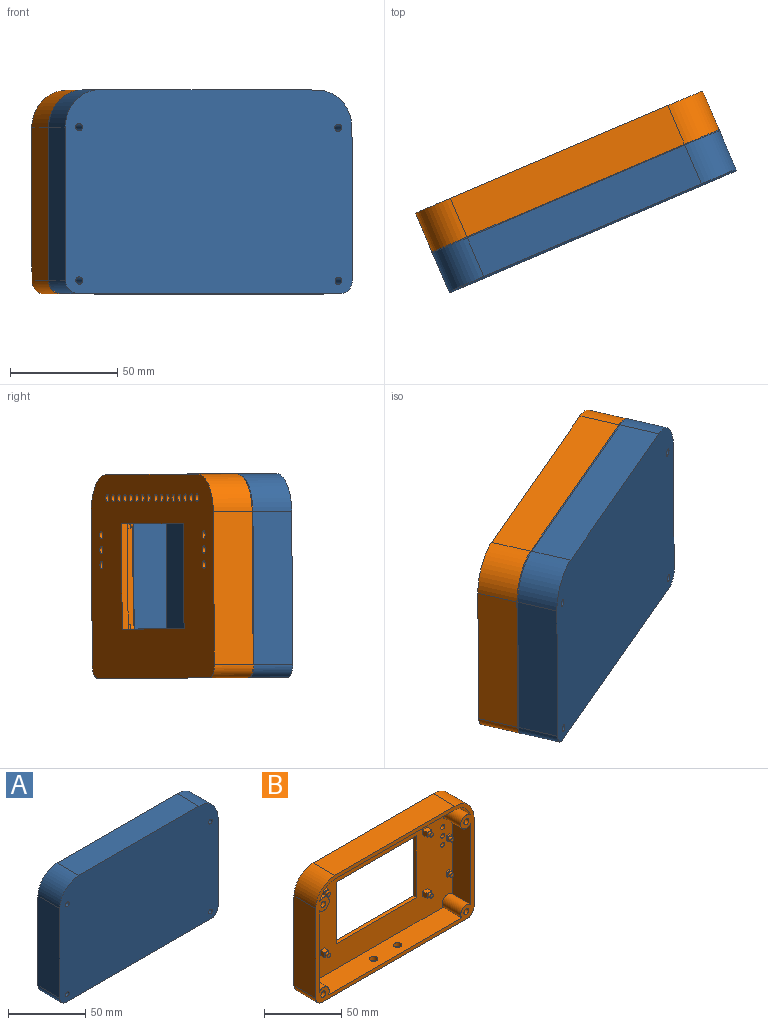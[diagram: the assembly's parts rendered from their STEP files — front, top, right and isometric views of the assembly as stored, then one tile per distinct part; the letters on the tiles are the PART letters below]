
ASSEMBLY  parts=2 mates=1
PART A: 51 faces, bbox 145x20x94.7 mm
  f0: plane 40x17mm, normal (0,0,1), area 624mm2, adj f3,f23,f28,f29,f33,f34,f35,f36
  f1: plane 36x17mm, normal (0,0,-1), area 556mm2, adj f3,f30,f31,f32,f33,f34,f35,f36
  f2: plane 41.8x17mm, normal (0,0,1), area 710.6mm2, adj f3,f23,f26,f29
  f3: plane 145x94.7mm, normal (0,1,0), area 1590.6mm2, adj f0,f1,f2,f4,f5,f6,f7,f8
  f4: plane 110x20mm, normal (0,0,1), area 2200mm2, adj f3,f5,f11,f12
  f5: cylinder r=17.5mm len=20mm, axis (0,1,0), area 549.8mm2, adj f3,f4,f6,f12
  f6: plane 71.2x20mm, normal (-1,0,0), area 1424mm2, adj f3,f5,f7,f12
  f7: cylinder r=6mm len=20mm, axis (0,1,0), area 188.5mm2, adj f3,f6,f8,f12
  f8: plane 133x20mm, normal (0,0,-1), area 2048mm2, adj f3,f7,f9,f12,f30,f31,f32
  f9: cylinder r=6mm len=20mm, axis (0,1,0), area 188.5mm2, adj f3,f8,f10,f12
  f10: plane 71.2x20mm, normal (1,0,0), area 1424mm2, adj f3,f9,f11,f12
  f11: cylinder r=17.5mm len=20mm, axis (0,1,0), area 549.8mm2, adj f3,f4,f10,f12
  f12: plane 145x94.7mm, normal (0,-1,0), area 13548.3mm2, adj f4,f5,f6,f7,f8,f9,f10,f11
  f13: cylinder r=1.7mm len=20mm, axis (0,-1,0), area 213.6mm2, adj f3,f12
  f14: cylinder r=1.7mm len=20mm, axis (0,-1,0), area 213.6mm2, adj f3,f12
  f15: cylinder r=1.7mm len=20mm, axis (0,-1,0), area 213.6mm2, adj f3,f12
  f16: cylinder r=1.7mm len=20mm, axis (0,-1,0), area 213.6mm2, adj f3,f12
  f17: plane 110x17mm, normal (0,0,-1), area 1870mm2, adj f3,f18,f22,f23
  f18: cylinder r=14.5mm len=17mm, axis (0,1,0), area 337.8mm2, adj f3,f17,f23,f24
  f19: plane 66.36x17mm, normal (1,0,0), area 1128.2mm2, adj f3,f23,f24,f26
  f20: plane 41.8x17mm, normal (0,0,1), area 710.6mm2, adj f3,f23,f25,f28
  f21: plane 66.36x17mm, normal (-1,0,0), area 1128.2mm2, adj f3,f23,f25,f27
  f22: cylinder r=14.5mm len=17mm, axis (0,1,0), area 337.8mm2, adj f3,f17,f23,f27
  f23: plane 139x88.7mm, normal (0,1,0), area 11201.7mm2, adj f0,f2,f17,f18,f19,f20,f21,f22
  f24: cylinder r=4.7mm len=17mm, axis (0,-1,0), area 405mm2, adj f3,f18,f19,f23
  f25: cylinder r=4.7mm len=17mm, axis (0,-1,0), area 260mm2, adj f3,f20,f21,f23
  f26: cylinder r=4.7mm len=17mm, axis (0,-1,0), area 260mm2, adj f2,f3,f19,f23
  f27: cylinder r=4.7mm len=17mm, axis (0,-1,0), area 405mm2, adj f3,f21,f22,f23
  f28: plane 17x17mm, normal (1,0,0), area 289mm2, adj f0,f3,f20,f23
  f29: plane 17x17mm, normal (-1,0,0), area 289mm2, adj f0,f2,f3,f23
  f30: plane 18x17mm, normal (1,0,0), area 306mm2, adj f1,f3,f8,f32
  f31: plane 18x17mm, normal (-1,0,0), area 306mm2, adj f1,f3,f8,f32
  f32: plane 36x18mm, normal (0,1,0), area 648mm2, adj f1,f8,f30,f31
  f33: plane 7x2mm, normal (0,1,0), area 14mm2, adj f0,f1,f34,f36
  f34: plane 4x2mm, normal (1,0,0), area 8mm2, adj f0,f1,f33,f35
  f35: plane 7x2mm, normal (0,-1,0), area 14mm2, adj f0,f1,f34,f36
  f36: plane 4x2mm, normal (-1,0,0), area 8mm2, adj f0,f1,f33,f35
  f37: plane 7x2mm, normal (0,1,0), area 14mm2, adj f0,f1,f38,f40
  f38: plane 4x2mm, normal (1,0,0), area 8mm2, adj f0,f1,f37,f39
  f39: plane 7x2mm, normal (0,-1,0), area 14mm2, adj f0,f1,f38,f40
  f40: plane 4x2mm, normal (-1,0,0), area 8mm2, adj f0,f1,f37,f39
  f41: plane 18x4mm, normal (0,0,-1), area 72mm2, adj f23,f42,f44,f45
  f42: plane 4x3mm, normal (-1,0,0), area 12mm2, adj f23,f41,f43,f45
  f43: plane 18x4mm, normal (0,0,1), area 72mm2, adj f23,f42,f44,f45
  f44: plane 4x3mm, normal (1,0,0), area 12mm2, adj f23,f41,f43,f45
  f45: plane 18x3mm, normal (0,1,0), area 54mm2, adj f41,f42,f43,f44
  f46: plane 4x3mm, normal (1,0,0), area 12mm2, adj f23,f47,f49,f50
  f47: plane 18x4mm, normal (0,0,-1), area 72mm2, adj f23,f46,f48,f50
  f48: plane 4x3mm, normal (-1,0,0), area 12mm2, adj f23,f47,f49,f50
  f49: plane 18x4mm, normal (0,0,1), area 72mm2, adj f23,f46,f48,f50
  f50: plane 18x3mm, normal (0,1,0), area 54mm2, adj f46,f47,f48,f49
PART B: 141 faces, bbox 145x20x94.7 mm
  f0: plane 145x94.7mm, normal (0,1,0), area 9777.3mm2, adj f2,f3,f4,f5,f6,f7,f8,f9
  f1: plane 139x88.7mm, normal (0,-1,0), area 7978.6mm2, adj f19,f20,f21,f22,f23,f24,f25,f26
  f2: plane 110x20mm, normal (0,0,1), area 2200mm2, adj f0,f3,f9,f10
  f3: cylinder r=17.5mm len=20mm, axis (0,1,0), area 549.8mm2, adj f0,f2,f4,f10
  f4: plane 71.2x20mm, normal (-1,0,0), area 1424mm2, adj f0,f3,f5,f10
  f5: cylinder r=6mm len=20mm, axis (0,1,0), area 188.5mm2, adj f0,f4,f6,f10
  f6: plane 133x20mm, normal (0,0,-1), area 2612.5mm2, adj f0,f5,f7,f10,f55,f56
  f7: cylinder r=6mm len=20mm, axis (0,1,0), area 188.5mm2, adj f0,f6,f8,f10
  f8: plane 71.2x20mm, normal (1,0,0), area 1424mm2, adj f0,f7,f9,f10
  f9: cylinder r=17.5mm len=20mm, axis (0,1,0), area 549.8mm2, adj f0,f2,f8,f10
  f10: plane 145x94.7mm, normal (0,-1,0), area 1575.1mm2, adj f2,f3,f4,f5,f6,f7,f8,f9
  f11: cone r=0mm half-angle=59deg, axis (0,-1,0), area 18.6mm2, adj f12
  f12: cylinder r=2.25mm len=17mm, axis (0,-1,0), area 240.3mm2, adj f10,f11
  f13: cone r=0mm half-angle=59deg, axis (0,-1,0), area 18.6mm2, adj f14
  f14: cylinder r=2.25mm len=17mm, axis (0,-1,0), area 240.3mm2, adj f10,f13
  f15: cone r=0mm half-angle=59deg, axis (0,-1,0), area 18.6mm2, adj f16
  f16: cylinder r=2.25mm len=17mm, axis (0,-1,0), area 240.3mm2, adj f10,f15
  f17: cone r=0mm half-angle=59deg, axis (0,-1,0), area 18.6mm2, adj f18
  f18: cylinder r=2.25mm len=17mm, axis (0,-1,0), area 240.3mm2, adj f10,f17
  f19: cylinder r=5.25mm len=17mm, axis (0,-1,0), area 269.7mm2, adj f1,f10,f23,f24
  f20: plane 110x17mm, normal (0,0,-1), area 1870mm2, adj f1,f10,f21,f25
  f21: cylinder r=14.5mm len=17mm, axis (0,1,0), area 319.1mm2, adj f1,f10,f20,f26
  f22: plane 64.5x17mm, normal (1,0,0), area 1096.5mm2, adj f1,f10,f26,f28
  f23: plane 122.25x17mm, normal (0,0,1), area 2030.7mm2, adj f1,f10,f19,f28,f55,f56
  f24: plane 64.5x17mm, normal (-1,0,0), area 1096.5mm2, adj f1,f10,f19,f27
  f25: cylinder r=14.5mm len=17mm, axis (0,1,0), area 319.1mm2, adj f1,f10,f20,f27
  f26: cylinder r=5.25mm len=17mm, axis (0,-1,0), area 421.7mm2, adj f1,f10,f21,f22
  f27: cylinder r=5.25mm len=17mm, axis (0,-1,0), area 421.7mm2, adj f1,f10,f24,f25
  f28: cylinder r=5.25mm len=17mm, axis (0,-1,0), area 269.7mm2, adj f1,f10,f22,f23
  f29: cylinder r=1.75mm len=3.5mm, axis (0,-1,0), area 33mm2, adj f0,f1
  f30: cylinder r=1.75mm len=3.5mm, axis (0,-1,0), area 33mm2, adj f0,f1
  f31: cylinder r=1.75mm len=3.5mm, axis (0,-1,0), area 33mm2, adj f0,f1
  f32: cylinder r=1.75mm len=3.5mm, axis (0,-1,0), area 33mm2, adj f0,f1
  f33: cylinder r=1.75mm len=3.5mm, axis (0,-1,0), area 33mm2, adj f0,f1
  f34: cylinder r=1.75mm len=3.5mm, axis (0,-1,0), area 33mm2, adj f0,f1
  f35: cylinder r=1.75mm len=3.5mm, axis (0,-1,0), area 33mm2, adj f0,f1
  f36: cylinder r=1.75mm len=3.5mm, axis (0,-1,0), area 33mm2, adj f0,f1
  f37: cylinder r=1.75mm len=3.5mm, axis (0,-1,0), area 33mm2, adj f0,f1
  f38: cylinder r=1.75mm len=3.5mm, axis (0,-1,0), area 33mm2, adj f0,f1
  f39: cylinder r=1.75mm len=3.5mm, axis (0,-1,0), area 33mm2, adj f0,f1
  f40: cylinder r=1.75mm len=3.5mm, axis (0,-1,0), area 33mm2, adj f0,f1
  f41: cylinder r=1.75mm len=3.5mm, axis (0,-1,0), area 33mm2, adj f0,f1
  f42: cylinder r=1.75mm len=3.5mm, axis (0,-1,0), area 33mm2, adj f0,f1
  f43: cylinder r=1.75mm len=3.5mm, axis (0,-1,0), area 33mm2, adj f0,f1
  f44: cylinder r=1.75mm len=3.5mm, axis (0,-1,0), area 33mm2, adj f0,f1
  f45: cylinder r=1.75mm len=3.5mm, axis (0,-1,0), area 33mm2, adj f0,f1
  f46: cylinder r=1.75mm len=3.5mm, axis (0,-1,0), area 33mm2, adj f0,f1
  f47: cylinder r=1.75mm len=3.5mm, axis (0,-1,0), area 33mm2, adj f0,f1
  f48: cylinder r=1.75mm len=3.5mm, axis (0,-1,0), area 33mm2, adj f0,f1
  f49: cylinder r=1.75mm len=3.5mm, axis (0,-1,0), area 33mm2, adj f0,f1
  f50: cylinder r=1.75mm len=3.5mm, axis (0,-1,0), area 33mm2, adj f0,f1
  f51: plane 73.44x3mm, normal (0,0,-1), area 220.3mm2, adj f0,f1,f52,f54
  f52: plane 48.96x3mm, normal (1,0,0), area 146.9mm2, adj f0,f1,f51,f53
  f53: plane 73.44x3mm, normal (0,0,1), area 220.3mm2, adj f0,f1,f52,f54
  f54: plane 48.96x3mm, normal (-1,0,0), area 146.9mm2, adj f0,f1,f51,f53
  f55: cylinder r=2.75mm len=5.5mm, axis (0,0,-1), area 51.8mm2, adj f6,f23
  f56: cylinder r=2.75mm len=5.5mm, axis (0,0,-1), area 51.8mm2, adj f6,f23
  f57: plane 3x1.5mm, normal (0,0,-1), area 4.5mm2, adj f1,f58,f60,f61
  f58: plane 4x1.5mm, normal (1,0,0), area 6mm2, adj f1,f57,f59,f61
  f59: plane 3x1.5mm, normal (0,0,1), area 4.5mm2, adj f1,f58,f60,f61
  f60: plane 4x1.5mm, normal (-1,0,0), area 6mm2, adj f1,f57,f59,f61
  f61: plane 4x3mm, normal (0,-1,0), area 5mm2, adj f57,f58,f59,f60,f99
  f62: plane 3x1.5mm, normal (0,0,-1), area 4.5mm2, adj f1,f63,f65,f66
  f63: plane 4x1.5mm, normal (1,0,0), area 6mm2, adj f1,f62,f64,f66
  f64: plane 3x1.5mm, normal (0,0,1), area 4.5mm2, adj f1,f63,f65,f66
  f65: plane 4x1.5mm, normal (-1,0,0), area 6mm2, adj f1,f62,f64,f66
  f66: plane 4x3mm, normal (0,-1,0), area 5mm2, adj f62,f63,f64,f65,f97
  f67: plane 3x1.5mm, normal (0,0,-1), area 4.5mm2, adj f1,f68,f70,f71
  f68: plane 4x1.5mm, normal (1,0,0), area 6mm2, adj f1,f67,f69,f71
  f69: plane 3x1.5mm, normal (0,0,1), area 4.5mm2, adj f1,f68,f70,f71
  f70: plane 4x1.5mm, normal (-1,0,0), area 6mm2, adj f1,f67,f69,f71
  f71: plane 4x3mm, normal (0,-1,0), area 5mm2, adj f67,f68,f69,f70,f103
  f72: plane 3x1.5mm, normal (0,0,-1), area 4.5mm2, adj f1,f73,f75,f76
  f73: plane 4x1.5mm, normal (1,0,0), area 6mm2, adj f1,f72,f74,f76
  f74: plane 3x1.5mm, normal (0,0,1), area 4.5mm2, adj f1,f73,f75,f76
  f75: plane 4x1.5mm, normal (-1,0,0), area 6mm2, adj f1,f72,f74,f76
  f76: plane 4x3mm, normal (0,-1,0), area 5mm2, adj f72,f73,f74,f75,f101
  f77: plane 4x1.5mm, normal (0,0,-1), area 6mm2, adj f1,f78,f80,f81
  f78: plane 3x1.5mm, normal (1,0,0), area 4.5mm2, adj f1,f77,f79,f81
  f79: plane 4x1.5mm, normal (0,0,1), area 6mm2, adj f1,f78,f80,f81
  f80: plane 3x1.5mm, normal (-1,0,0), area 4.5mm2, adj f1,f77,f79,f81
  f81: plane 4x3mm, normal (0,-1,0), area 5mm2, adj f77,f78,f79,f80,f111
  f82: plane 4x1.5mm, normal (0,0,-1), area 6mm2, adj f1,f83,f85,f86
  f83: plane 3x1.5mm, normal (1,0,0), area 4.5mm2, adj f1,f82,f84,f86
  f84: plane 4x1.5mm, normal (0,0,1), area 6mm2, adj f1,f83,f85,f86
  f85: plane 3x1.5mm, normal (-1,0,0), area 4.5mm2, adj f1,f82,f84,f86
  f86: plane 4x3mm, normal (0,-1,0), area 5mm2, adj f82,f83,f84,f85,f105
  f87: plane 4x1.5mm, normal (0,0,-1), area 6mm2, adj f1,f88,f90,f91
  f88: plane 3x1.5mm, normal (1,0,0), area 4.5mm2, adj f1,f87,f89,f91
  f89: plane 4x1.5mm, normal (0,0,1), area 6mm2, adj f1,f88,f90,f91
  f90: plane 3x1.5mm, normal (-1,0,0), area 4.5mm2, adj f1,f87,f89,f91
  f91: plane 4x3mm, normal (0,-1,0), area 5mm2, adj f87,f88,f89,f90,f107
  f92: plane 4x1.5mm, normal (0,0,-1), area 6mm2, adj f1,f93,f95,f96
  f93: plane 3x1.5mm, normal (1,0,0), area 4.5mm2, adj f1,f92,f94,f96
  f94: plane 4x1.5mm, normal (0,0,1), area 6mm2, adj f1,f93,f95,f96
  f95: plane 3x1.5mm, normal (-1,0,0), area 4.5mm2, adj f1,f92,f94,f96
  f96: plane 4x3mm, normal (0,-1,0), area 5mm2, adj f92,f93,f94,f95,f109
  f97: cylinder r=1.5mm len=2.99mm, axis (0,1,0), area 23.5mm2, adj f66,f98
  f98: plane 2.99x2.99mm, normal (0,-1,0), area 7mm2, adj f97
  f99: cylinder r=1.5mm len=2.99mm, axis (0,1,0), area 23.5mm2, adj f61,f100
  f100: plane 2.99x2.99mm, normal (0,-1,0), area 7mm2, adj f99
  f101: cylinder r=1.5mm len=2.99mm, axis (0,1,0), area 23.5mm2, adj f76,f102
  f102: plane 2.99x2.99mm, normal (0,-1,0), area 7mm2, adj f101
  f103: cylinder r=1.5mm len=2.99mm, axis (0,1,0), area 23.5mm2, adj f71,f104
  f104: plane 2.99x2.99mm, normal (0,-1,0), area 7mm2, adj f103
  f105: cylinder r=1.5mm len=2.99mm, axis (0,1,0), area 23.5mm2, adj f86,f106
  f106: plane 2.99x2.99mm, normal (0,-1,0), area 7mm2, adj f105
  f107: cylinder r=1.5mm len=2.99mm, axis (0,1,0), area 23.5mm2, adj f91,f108
  f108: plane 2.99x2.99mm, normal (0,-1,0), area 7mm2, adj f107
  f109: cylinder r=1.5mm len=2.99mm, axis (0,1,0), area 23.5mm2, adj f96,f110
  f110: plane 2.99x2.99mm, normal (0,-1,0), area 7mm2, adj f109
  f111: cylinder r=1.5mm len=2.99mm, axis (0,1,0), area 23.5mm2, adj f81,f112
  f112: plane 2.99x2.99mm, normal (0,-1,0), area 7mm2, adj f111
  f113: plane 4x3.85mm, normal (0,0,-1), area 15.4mm2, adj f1,f114,f116,f117
  f114: plane 4x3.85mm, normal (1,0,0), area 15.4mm2, adj f1,f113,f115,f117
  f115: plane 4x3.85mm, normal (0,0,1), area 15.4mm2, adj f1,f114,f116,f117
  f116: plane 4x3.85mm, normal (-1,0,0), area 15.4mm2, adj f1,f113,f115,f117
  f117: plane 4x4mm, normal (0,-1,0), area 8.5mm2, adj f113,f114,f115,f116,f133
  f118: plane 4x3.85mm, normal (0,0,1), area 15.4mm2, adj f1,f119,f121,f122
  f119: plane 4x3.85mm, normal (-1,0,0), area 15.4mm2, adj f1,f118,f120,f122
  f120: plane 4x3.85mm, normal (0,0,-1), area 15.4mm2, adj f1,f119,f121,f122
  f121: plane 4x3.85mm, normal (1,0,0), area 15.4mm2, adj f1,f118,f120,f122
  f122: plane 4x4mm, normal (0,-1,0), area 8.5mm2, adj f118,f119,f120,f121,f135
  f123: plane 4x3.85mm, normal (0,0,-1), area 15.4mm2, adj f1,f124,f126,f127
  f124: plane 4x3.85mm, normal (1,0,0), area 15.4mm2, adj f1,f123,f125,f127
  f125: plane 4x3.85mm, normal (0,0,1), area 15.4mm2, adj f1,f124,f126,f127
  f126: plane 4x3.85mm, normal (-1,0,0), area 15.4mm2, adj f1,f123,f125,f127
  f127: plane 4x4mm, normal (0,-1,0), area 8.5mm2, adj f123,f124,f125,f126,f137
  f128: plane 4x3.85mm, normal (0,0,-1), area 15.4mm2, adj f1,f129,f131,f132
  f129: plane 4x3.85mm, normal (1,0,0), area 15.4mm2, adj f1,f128,f130,f132
  f130: plane 4x3.85mm, normal (0,0,1), area 15.4mm2, adj f1,f129,f131,f132
  f131: plane 4x3.85mm, normal (-1,0,0), area 15.4mm2, adj f1,f128,f130,f132
  f132: plane 4x4mm, normal (0,-1,0), area 8.5mm2, adj f128,f129,f130,f131,f139
  f133: cylinder r=1.55mm len=3.1mm, axis (0,1,0), area 20.9mm2, adj f117,f134
  f134: plane 3.1x3.1mm, normal (0,-1,0), area 7.5mm2, adj f133
  f135: cylinder r=1.55mm len=3.1mm, axis (0,1,0), area 20.9mm2, adj f122,f136
  f136: plane 3.1x3.1mm, normal (0,-1,0), area 7.5mm2, adj f135
  f137: cylinder r=1.55mm len=3.1mm, axis (0,1,0), area 20.9mm2, adj f127,f138
  f138: plane 3.1x3.1mm, normal (0,-1,0), area 7.5mm2, adj f137
  f139: cylinder r=1.55mm len=3.1mm, axis (0,1,0), area 20.9mm2, adj f132,f140
  f140: plane 3.1x3.1mm, normal (0,-1,0), area 7.5mm2, adj f139
PLACE A rot(axis=(-0.02,0,1),23.1deg) t=(-6.04,-41.32,16.75)mm
PLACE B rot(axis=(-0.02,0,1),23.1deg) t=(-13.75,-23.27,16.55)mm
MATE parallel B.f13 <-> A.f16  axis (0.39,-0.92,0.01) through (54.3,-15.8,46.45)mm
